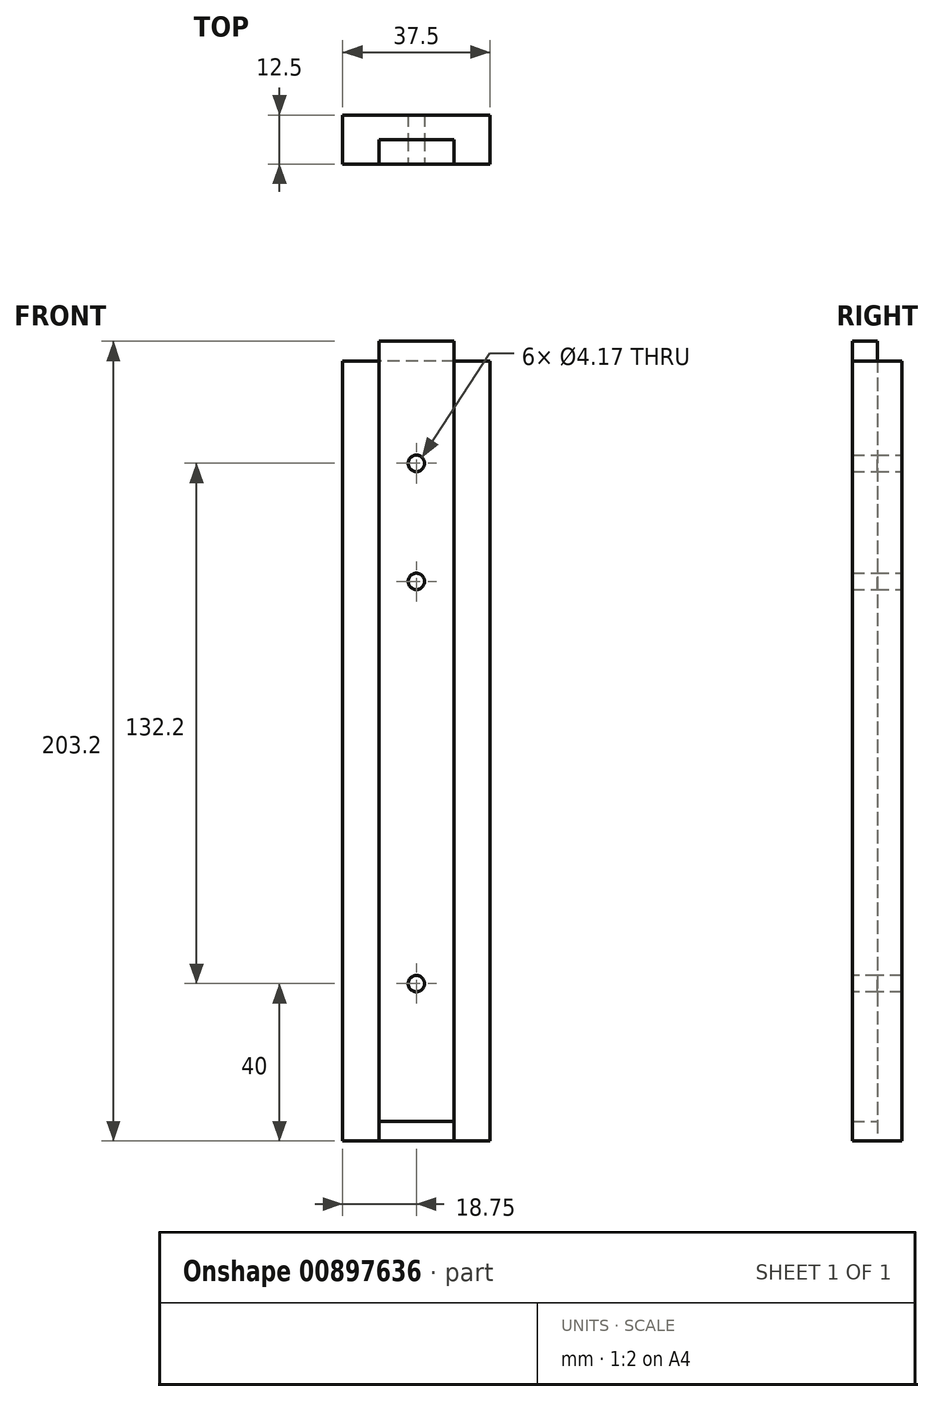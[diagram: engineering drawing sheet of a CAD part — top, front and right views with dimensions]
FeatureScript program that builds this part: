
annotation { "Feature Type Name" : "Feature", "Feature Type Description" : "" }
export const myFeature = defineFeature(function(context is Context, id is Id, definition is map)
    precondition{}
    {
        {
            var Q0;
            Q0=qCreatedBy(makeId("Right.planeOp"),FACE);
            var sketch = newSketch(context, id + "F0", { "sketchPlane" : qUnion([Q0])});
            skLineSegment(sketch, "E0.bottom", {"start": v(0, 0) * mm, "end": v(12.5, 0) * mm});
            skLineSegment(sketch, "E0.top", {"start": v(0, 198.2) * mm, "end": v(12.5, 198.2) * mm});
            skLineSegment(sketch, "E0.left", {"start": v(0, 0) * mm, "end": v(0, 198.2) * mm});
            skLineSegment(sketch, "E0.right", {"start": v(12.5, 0) * mm, "end": v(12.5, 198.2) * mm});
            skLineSegment(sketch, "E1", {"start": v(0, 5) * mm, "end": v(12.5, 5) * mm});
            skLineSegment(sketch, "E2", {"start": v(0, 198.2) * mm, "end": v(0, 203.2) * mm});
            skLineSegment(sketch, "E3", {"start": v(0, 203.2) * mm, "end": v(12.5, 203.2) * mm});
            skLineSegment(sketch, "E4", {"start": v(12.5, 203.2) * mm, "end": v(12.5, 198.2) * mm});
            skLineSegment(sketch, "E5", {"start": v(6.25, 203.2) * mm, "end": v(6.25, 5) * mm, "construction": true});
            skSolve(sketch);
        }
        {
            var Q0;
            Q0=qCreatedBy(makeId("Top.planeOp"),FACE);
            var sketch = newSketch(context, id + "F1", { "sketchPlane" : qUnion([Q0])});
            skLineSegment(sketch, "E6.bottom", {"start": v(0, 0) * mm, "end": v(-37.5, 0) * mm});
            skLineSegment(sketch, "E6.top", {"start": v(0, 12.5) * mm, "end": v(-37.5, 12.5) * mm});
            skLineSegment(sketch, "E6.left", {"start": v(0, 0) * mm, "end": v(0, 12.5) * mm});
            skLineSegment(sketch, "E6.right", {"start": v(-37.5, 0) * mm, "end": v(-37.5, 12.5) * mm});
            skLineSegment(sketch, "E7.0", {"start": v(-9.22, 0) * mm, "end": v(-9.22, 6.25) * mm});
            skLineSegment(sketch, "E7.1", {"start": v(-9.23, 6.25) * mm, "end": v(-28.27, 6.25) * mm});
            skLineSegment(sketch, "E7.2", {"start": v(-28.28, 0) * mm, "end": v(-28.28, 6.25) * mm});
            skLineSegment(sketch, "E8", {"start": v(-18.75, 6.25) * mm, "end": v(-18.75, 12.5) * mm, "construction": true});
            skSolve(sketch);
        }
        {
            var Q0;
            Q0=makeQuery(id+"F1.imprint","IMPRINT",FACE,{"disambiguationData":[TD([[makeQuery(id+"F1.imprint","IMPRINT",EDGE,{"derivedFrom":sQuery(id+"F1.wireOp",EDGE,"E6.top")}),1.0]])]});
            var Q1;
            Q1=sQuery(id+"F0.wireOp",VERTEX,"E0.top.start");
            extrude(context, id + "F2", {"entities" : qUnion([Q0]), "endBound" : BoundingType.UP_TO_VERTEX, "depth" : 25 * mm, "endBoundEntityVertex" : qUnion([Q1]), "offsetDistance" : 25 * mm});
        }
        {
            var Q0;
            {var subQ0=sQuery(id+"F1.wireOp",EDGE,"E7.0");Q0=makeQuery(id+"F1.imprint","IMPRINT",FACE,{"disambiguationData":[TD([[makeQuery(id+"F1.imprint","IMPRINT",EDGE,{"derivedFrom":subQ0}),1.0]])]});}
            var Q1;
            Q1=sQuery(id+"F0.wireOp",VERTEX,"E2.end");
            var Q2;
            Q2=sQuery(id+"F0.wireOp",VERTEX,"E1.start");
            extrude(context, id + "F3", {"entities" : qUnion([Q0]), "endBound" : BoundingType.UP_TO_VERTEX, "depth" : 25 * mm, "endBoundEntityVertex" : qUnion([Q1]), "offsetDistance" : 25 * mm, "hasSecondDirection" : true, "secondDirectionBound" : BoundingType.UP_TO_VERTEX, "secondDirectionOppositeDirection" : false, "secondDirectionDepth" : 25 * mm, "secondDirectionBoundEntityVertex" : qUnion([Q2])});
        }
        {
            var Q0;
            Q0=makeQuery(id+"F3.opExtrude","SWEPT_FACE",FACE,{"disambiguationData":[OSD([sQuery(id+"F1.wireOp",EDGE,"E6.bottom")])]});
            var sketch = newSketch(context, id + "F4", { "sketchPlane" : qUnion([Q0])});
            skLineSegment(sketch, "E9", {"start": v(-18.75, 203.2) * mm, "end": v(-18.75, 5) * mm, "construction": true});
            skCircle(sketch, "E10", {"center": v(-18.75, 40) * mm, "radius": 2.08 * mm});
            skSolve(sketch);
        }
        {
            var Q0;
            Q0=makeQuery(id+"F4.imprint","IMPRINT",FACE,{"disambiguationData":[TD([[makeQuery(id+"F4.imprint","IMPRINT",EDGE,{"derivedFrom":sQuery(id+"F4.wireOp",EDGE,"E10")}),1.0]])]});
            extrude(context, id + "F5", {"entities" : qUnion([Q0]), "operationType" : NewBodyOperationType.REMOVE, "endBound" : BoundingType.THROUGH_ALL, "oppositeDirection" : true, "depth" : 25 * mm, "offsetDistance" : 25 * mm});
        }
        {
            var Q0;
            Q0=makeQuery(id+"F2.opExtrude","SWEPT_FACE",FACE,{"disambiguationData":[OSD([sQuery(id+"F1.wireOp",EDGE,"E6.top")])]});
            var sketch = newSketch(context, id + "F6", { "sketchPlane" : qUnion([Q0])});
            skLineSegment(sketch, "E11", {"start": v(18.75, 198.2) * mm, "end": v(18.75, 0) * mm, "construction": true});
            skCircle(sketch, "E12", {"center": v(18.75, 142.2) * mm, "radius": 2.08 * mm});
            skCircle(sketch, "E13", {"center": v(18.75, 172.2) * mm, "radius": 2.08 * mm});
            skSolve(sketch);
        }
        {
            var Q0;
            Q0=makeQuery(id+"F6.imprint","IMPRINT",FACE,{"disambiguationData":[TD([[makeQuery(id+"F6.imprint","IMPRINT",EDGE,{"derivedFrom":sQuery(id+"F6.wireOp",EDGE,"E12")}),1.0]])]});
            var Q1;
            Q1=makeQuery(id+"F6.imprint","IMPRINT",FACE,{"disambiguationData":[TD([[makeQuery(id+"F6.imprint","IMPRINT",EDGE,{"derivedFrom":sQuery(id+"F6.wireOp",EDGE,"SsDHlxKf-cehi-i5MC-3QXJ-46OJaeq5sM60")}),1.0]])]});
            var Q2;
            Q2=makeQuery(id+"F6.imprint","IMPRINT",FACE,{"disambiguationData":[TD([[makeQuery(id+"F6.imprint","IMPRINT",EDGE,{"derivedFrom":sQuery(id+"F6.wireOp",EDGE,"E13")}),1.0]])]});
            extrude(context, id + "F7", {"entities" : qUnion([Q0, Q1, Q2]), "operationType" : NewBodyOperationType.REMOVE, "oppositeDirection" : true, "depth" : 25 * mm, "offsetDistance" : 25 * mm});
        }
    });
